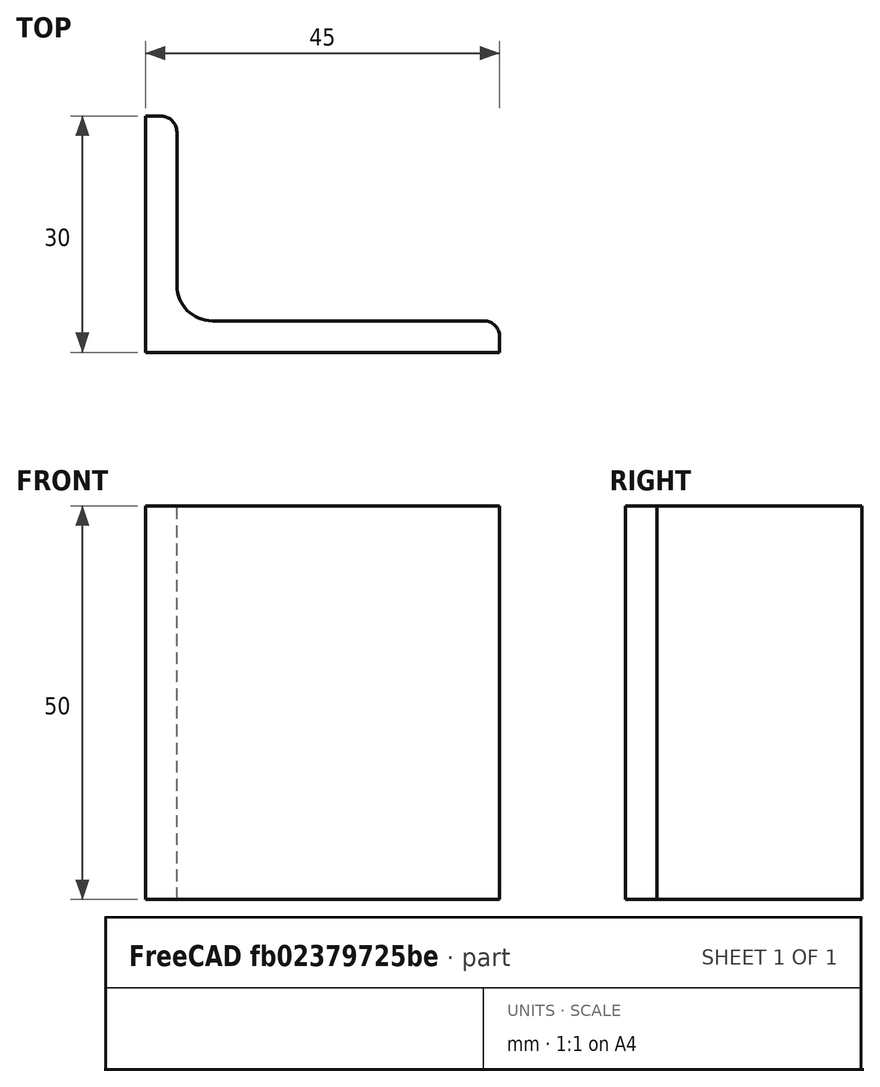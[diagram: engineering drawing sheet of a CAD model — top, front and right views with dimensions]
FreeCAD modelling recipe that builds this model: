
FCSTD DOCUMENT  (FreeCAD 0.15R4671 (Git))
Label: Angle Bar 45x30x4 EN10056 S235JR
License: All rights reserved
LicenseURL: http://en.wikipedia.org/wiki/All_rights_reserved
objects: Sketcher::SketchObject×1, Part::Extrusion×1
note: 2 computed .brp shape members not serialized (recipe doc carries the construction recipe); baked Part::Feature solids carry a one-line shape summary decoded from their .brp

FEATURE [Sketcher::SketchObject] Sketch
  sketch-geometry (9):
    g0: LineSegment StartX=0 StartY=0 StartZ=0 EndX=45 EndY=0 EndZ=0
    g1: LineSegment StartX=45 StartY=0 StartZ=0 EndX=45 EndY=2 EndZ=0
    g2: LineSegment StartX=43 StartY=4 StartZ=0 EndX=8.5 EndY=4 EndZ=0
    g3: LineSegment StartX=0 StartY=0 StartZ=0 EndX=0 EndY=30 EndZ=0
    g4: LineSegment StartX=0 StartY=30 StartZ=0 EndX=2 EndY=30 EndZ=0
    g5: LineSegment StartX=4 StartY=28 StartZ=0 EndX=4 EndY=8.5 EndZ=0
    g6: ArcOfCircle CenterX=8.5 CenterY=8.5 CenterZ=0 NormalX=0 NormalY=0 NormalZ=1 Radius=4.5 StartAngle=3.14159 EndAngle=4.71239
    g7: ArcOfCircle CenterX=2 CenterY=28 CenterZ=0 NormalX=0 NormalY=0 NormalZ=1 Radius=2 StartAngle=0 EndAngle=1.5708
    g8: ArcOfCircle CenterX=43 CenterY=2 CenterZ=0 NormalX=0 NormalY=0 NormalZ=1 Radius=2 StartAngle=0 EndAngle=1.5708
  constraints (23):
    c: Coincident(g0,g-1)
    c: Horizontal(g0)
    c: Coincident(g1,g0)
    c: Vertical(g1)
    c: Horizontal(g2)
    c: Coincident(g3,g-1)
    c: Vertical(g3)
    c: Coincident(g4,g3)
    c: Horizontal(g4)
    c: Vertical(g5)
    c: Tangent(g5,g6) = -1.5708
    c: Tangent(g2,g6) = 1.5708
    c: Tangent(g4,g7) = 1.5708
    c: Tangent(g5,g7) = 1.5708
    c: Tangent(g2,g8) = -1.5708
    c: Tangent(g1,g8) = -1.5708
    c: DistanceX(g0) = 45
    c: DistanceY(g3) = 30
    c: DistanceY(g0,g2) = 4
    c: DistanceX(g3,g5) = 4
    c: Radius(g6) = 4.5
    c: Radius(g8) = 2
    c: Radius(g7) = 2
FEATURE [Part::Extrusion] Extrude  label="Angle Bar 45x30x4 EN10056 S235JR"
  Base = -> Sketch
  Dir = (0,0,50)
  Solid = true
